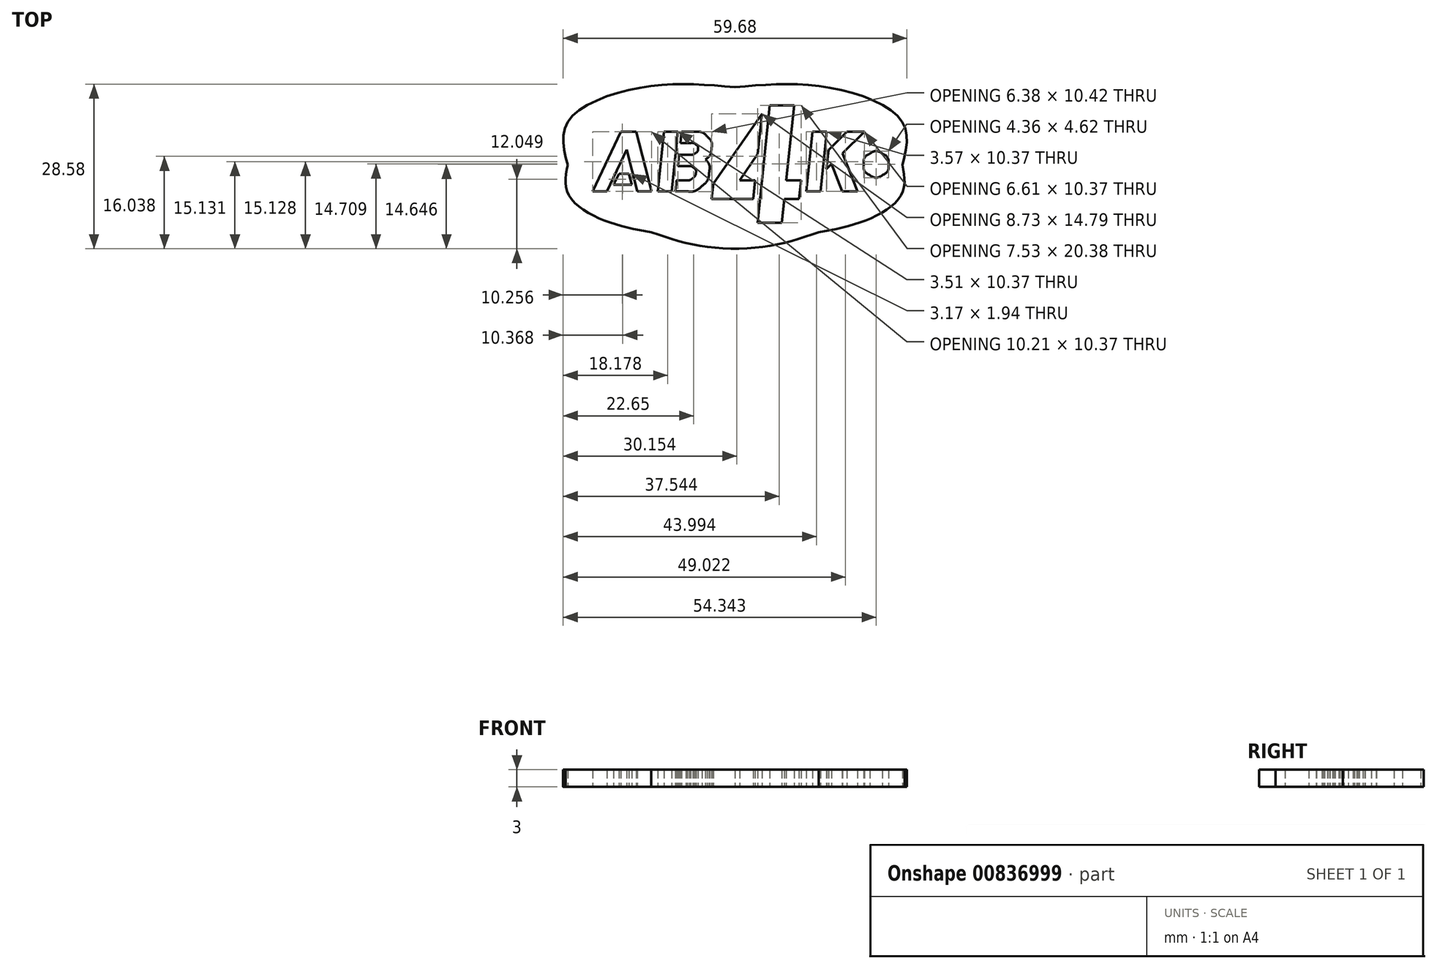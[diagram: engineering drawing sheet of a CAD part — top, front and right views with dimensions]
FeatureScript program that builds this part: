
annotation { "Feature Type Name" : "Feature", "Feature Type Description" : "" }
export const myFeature = defineFeature(function(context is Context, id is Id, definition is map)
    precondition{}
    {
        {
            var Q0;
            Q0=qCreatedBy(makeId("Top.planeOp"),FACE);
            var sketch = newSketch(context, id + "F0", { "sketchPlane" : qUnion([Q0])});
            skLineSegment(sketch, "E0", {"start": v(-22.2, -4.59) * mm, "end": v(-24.69, -4.59) * mm});
            skLineSegment(sketch, "E1", {"start": v(-24.69, -4.59) * mm, "end": v(-19.84, 5.78) * mm});
            skLineSegment(sketch, "E2", {"start": v(-19.84, 5.78) * mm, "end": v(-17.14, 5.78) * mm});
            skLineSegment(sketch, "E3", {"start": v(-17.14, 5.78) * mm, "end": v(-14.48, -4.59) * mm});
            skLineSegment(sketch, "E4", {"start": v(-14.48, -4.59) * mm, "end": v(-16.96, -4.59) * mm});
            skLineSegment(sketch, "E5", {"start": v(-16.96, -4.59) * mm, "end": v(-18.84, 2.66) * mm});
            skLineSegment(sketch, "E6", {"start": v(-18.84, 2.66) * mm, "end": v(-22.2, -4.59) * mm});
            skLineSegment(sketch, "E7", {"start": v(-21.06, -3.45) * mm, "end": v(-20.14, -1.51) * mm});
            skLineSegment(sketch, "E8", {"start": v(-20.14, -1.51) * mm, "end": v(-18.4, -1.51) * mm});
            skLineSegment(sketch, "E9", {"start": v(-18.4, -1.51) * mm, "end": v(-17.89, -3.45) * mm});
            skLineSegment(sketch, "E10", {"start": v(-17.89, -3.45) * mm, "end": v(-21.06, -3.45) * mm});
            skLineSegment(sketch, "E11", {"start": v(-9.71, 1.77) * mm, "end": v(-7.96, 1.77) * mm});
            skLineSegment(sketch, "E12", {"start": v(-7.69, 3.84) * mm, "end": v(-9.5, 3.84) * mm});
            skLineSegment(sketch, "E13", {"start": v(-9.5, 3.84) * mm, "end": v(-9.3, 5.79) * mm});
            skLineSegment(sketch, "E14", {"start": v(-9.3, 5.79) * mm, "end": v(-7.03, 5.79) * mm});
            skLineSegment(sketch, "E15", {"start": v(-8.27, -4.59) * mm, "end": v(-10.38, -4.59) * mm});
            skLineSegment(sketch, "E16", {"start": v(-10.38, -4.59) * mm, "end": v(-10.18, -2.67) * mm});
            skLineSegment(sketch, "E17", {"start": v(-10.18, -2.67) * mm, "end": v(-8.53, -2.67) * mm});
            skLineSegment(sketch, "E18", {"start": v(-8.27, -0.18) * mm, "end": v(-9.91, -0.18) * mm});
            skLineSegment(sketch, "E19", {"start": v(-9.91, -0.18) * mm, "end": v(-9.71, 1.77) * mm});
            skLineSegment(sketch, "E20", {"start": v(-11, -4.59) * mm, "end": v(-13.42, -4.59) * mm});
            skLineSegment(sketch, "E21", {"start": v(-13.42, -4.59) * mm, "end": v(-12.33, 5.79) * mm});
            skLineSegment(sketch, "E22", {"start": v(-12.33, 5.79) * mm, "end": v(-9.9, 5.79) * mm});
            skLineSegment(sketch, "E23", {"start": v(-9.9, 5.79) * mm, "end": v(-11, -4.59) * mm});
            skLineSegment(sketch, "E24", {"start": v(6.04, 10.37) * mm, "end": v(10.26, 10.37) * mm});
            skLineSegment(sketch, "E25", {"start": v(10.26, 10.37) * mm, "end": v(8.91, -2.63) * mm});
            skLineSegment(sketch, "E26", {"start": v(8.91, -2.63) * mm, "end": v(11.47, -2.63) * mm});
            skLineSegment(sketch, "E27", {"start": v(11.47, -2.63) * mm, "end": v(11.13, -5.89) * mm});
            skLineSegment(sketch, "E28", {"start": v(11.13, -5.89) * mm, "end": v(8.57, -5.89) * mm});
            skLineSegment(sketch, "E29", {"start": v(8.57, -5.89) * mm, "end": v(8.14, -10.01) * mm});
            skLineSegment(sketch, "E30", {"start": v(8.14, -10.01) * mm, "end": v(3.94, -10.01) * mm});
            skLineSegment(sketch, "E31", {"start": v(3.94, -10.01) * mm, "end": v(6.04, 10.37) * mm});
            skLineSegment(sketch, "E32", {"start": v(3.95, 1.94) * mm, "end": v(0.81, -2.63) * mm});
            skLineSegment(sketch, "E33", {"start": v(0.81, -2.63) * mm, "end": v(3.48, -2.63) * mm});
            skLineSegment(sketch, "E34", {"start": v(3.48, -2.63) * mm, "end": v(3.14, -5.89) * mm});
            skLineSegment(sketch, "E35", {"start": v(3.14, -5.89) * mm, "end": v(-4.05, -5.89) * mm});
            skLineSegment(sketch, "E36", {"start": v(-4.05, -5.89) * mm, "end": v(-3.76, -3.2) * mm});
            skLineSegment(sketch, "E37", {"start": v(-3.76, -3.2) * mm, "end": v(4.68, 8.9) * mm});
            skLineSegment(sketch, "E38", {"start": v(4.68, 8.9) * mm, "end": v(3.95, 1.94) * mm});
            skLineSegment(sketch, "E39", {"start": v(16.23, 2.63) * mm, "end": v(19.4, 5.78) * mm});
            skLineSegment(sketch, "E40", {"start": v(19.4, 5.78) * mm, "end": v(22.48, 5.78) * mm});
            skLineSegment(sketch, "E41", {"start": v(22.48, 5.78) * mm, "end": v(18.65, 2.06) * mm});
            skLineSegment(sketch, "E42", {"start": v(18.65, 2.06) * mm, "end": v(21.28, -4.59) * mm});
            skLineSegment(sketch, "E43", {"start": v(21.28, -4.59) * mm, "end": v(18.61, -4.59) * mm});
            skLineSegment(sketch, "E44", {"start": v(18.61, -4.59) * mm, "end": v(16.75, 0.17) * mm});
            skLineSegment(sketch, "E45", {"start": v(16.75, 0.17) * mm, "end": v(15.88, -0.68) * mm});
            skLineSegment(sketch, "E46", {"start": v(15.88, -0.68) * mm, "end": v(16.23, 2.63) * mm});
            skLineSegment(sketch, "E47", {"start": v(14.85, -4.59) * mm, "end": v(12.37, -4.59) * mm});
            skLineSegment(sketch, "E48", {"start": v(12.37, -4.59) * mm, "end": v(13.46, 5.78) * mm});
            skLineSegment(sketch, "E49", {"start": v(13.46, 5.78) * mm, "end": v(15.94, 5.78) * mm});
            skLineSegment(sketch, "E50", {"start": v(15.94, 5.78) * mm, "end": v(14.85, -4.59) * mm});
            skFitSpline(sketch, "E51", {"points": [v(29.05, 0) * mm, v(29.05, -4.83) * mm, v(23.52, -9.29) * mm, v(14.53, -11.7) * mm]});
            skFitSpline(sketch, "E52", {"points": [v(14.53, -11.7) * mm, v(5.54, -14.12) * mm, v(-5.54, -14.12) * mm, v(-14.53, -11.7) * mm]});
            skFitSpline(sketch, "E53", {"points": [v(-14.53, -11.7) * mm, v(-23.52, -9.29) * mm, v(-29.05, -4.83) * mm, v(-29.05, 0) * mm]});
            skFitSpline(sketch, "E54", {"points": [v(-29.05, 0) * mm, v(-29.05, 7.46) * mm, v(-16.05, 13.51) * mm, v(0, 13.51) * mm]});
            skFitSpline(sketch, "E55", {"points": [v(0, 13.51) * mm, v(16.05, 13.51) * mm, v(29.05, 7.46) * mm, v(29.05, 0) * mm]});
            skFitSpline(sketch, "E56", {"points": [v(26.66, 0.12) * mm, v(26.66, -0.65) * mm, v(26.25, -1.36) * mm, v(25.58, -1.75) * mm]});
            skFitSpline(sketch, "E57", {"points": [v(25.58, -1.75) * mm, v(24.91, -2.13) * mm, v(24.1, -2.13) * mm, v(23.43, -1.75) * mm]});
            skFitSpline(sketch, "E58", {"points": [v(23.43, -1.75) * mm, v(22.76, -1.36) * mm, v(22.35, -0.65) * mm, v(22.35, 0.12) * mm]});
            skFitSpline(sketch, "E59", {"points": [v(22.35, 0.12) * mm, v(22.35, 0.89) * mm, v(22.76, 1.6) * mm, v(23.43, 1.98) * mm]});
            skFitSpline(sketch, "E60", {"points": [v(23.43, 1.98) * mm, v(24.1, 2.37) * mm, v(24.91, 2.37) * mm, v(25.58, 1.98) * mm]});
            skFitSpline(sketch, "E61", {"points": [v(25.58, 1.98) * mm, v(26.25, 1.6) * mm, v(26.66, 0.89) * mm, v(26.66, 0.12) * mm]});
            skFitSpline(sketch, "E62", {"points": [v(-7.96, 1.77) * mm, v(-7.56, 1.77) * mm, v(-7.21, 1.86) * mm, v(-6.92, 2.04) * mm]});
            skFitSpline(sketch, "E63", {"points": [v(-6.92, 2.04) * mm, v(-6.63, 2.22) * mm, v(-6.47, 2.45) * mm, v(-6.44, 2.73) * mm]});
            skFitSpline(sketch, "E64", {"points": [v(-6.44, 2.73) * mm, v(-6.4, 3.05) * mm, v(-6.5, 3.31) * mm, v(-6.75, 3.52) * mm]});
            skFitSpline(sketch, "E65", {"points": [v(-6.75, 3.52) * mm, v(-7, 3.74) * mm, v(-7.31, 3.84) * mm, v(-7.69, 3.84) * mm]});
            skFitSpline(sketch, "E66", {"points": [v(-7.03, 5.79) * mm, v(-6.12, 5.79) * mm, v(-5.38, 5.5) * mm, v(-4.81, 4.92) * mm]});
            skFitSpline(sketch, "E67", {"points": [v(-4.81, 4.92) * mm, v(-4.25, 4.35) * mm, v(-4, 3.66) * mm, v(-4.1, 2.86) * mm]});
            skFitSpline(sketch, "E68", {"points": [v(-4.1, 2.86) * mm, v(-4.17, 2.1) * mm, v(-4.52, 1.46) * mm, v(-5.13, 0.96) * mm]});
            skFitSpline(sketch, "E69", {"points": [v(-5.13, 0.96) * mm, v(-4.61, 0.37) * mm, v(-4.4, -0.4) * mm, v(-4.5, -1.33) * mm]});
            skFitSpline(sketch, "E70", {"points": [v(-4.5, -1.33) * mm, v(-4.6, -2.22) * mm, v(-5, -2.98) * mm, v(-5.7, -3.62) * mm]});
            skFitSpline(sketch, "E71", {"points": [v(-5.7, -3.62) * mm, v(-6.44, -4.26) * mm, v(-7.3, -4.59) * mm, v(-8.27, -4.59) * mm]});
            skFitSpline(sketch, "E72", {"points": [v(-8.53, -2.67) * mm, v(-8.08, -2.67) * mm, v(-7.68, -2.54) * mm, v(-7.34, -2.29) * mm]});
            skFitSpline(sketch, "E73", {"points": [v(-7.34, -2.29) * mm, v(-7.03, -2.03) * mm, v(-6.84, -1.74) * mm, v(-6.79, -1.4) * mm]});
            skFitSpline(sketch, "E74", {"points": [v(-6.79, -1.4) * mm, v(-6.76, -1.03) * mm, v(-6.87, -0.74) * mm, v(-7.14, -0.52) * mm]});
            skFitSpline(sketch, "E75", {"points": [v(-7.14, -0.52) * mm, v(-7.42, -0.3) * mm, v(-7.8, -0.18) * mm, v(-8.27, -0.18) * mm]});
            skSolve(sketch);
        }
        {
            var Q0;
            Q0=makeQuery(id+"F0.imprint","IMPRINT",FACE,{"disambiguationData":[TD([[makeQuery(id+"F0.imprint","IMPRINT",EDGE,{"derivedFrom":sQuery(id+"F0.wireOp",EDGE,"E0")}),1.0]])]});
            extrude(context, id + "F1", {"entities" : qUnion([Q0]), "depth" : 3 * mm, "offsetDistance" : 25 * mm});
        }
    });
